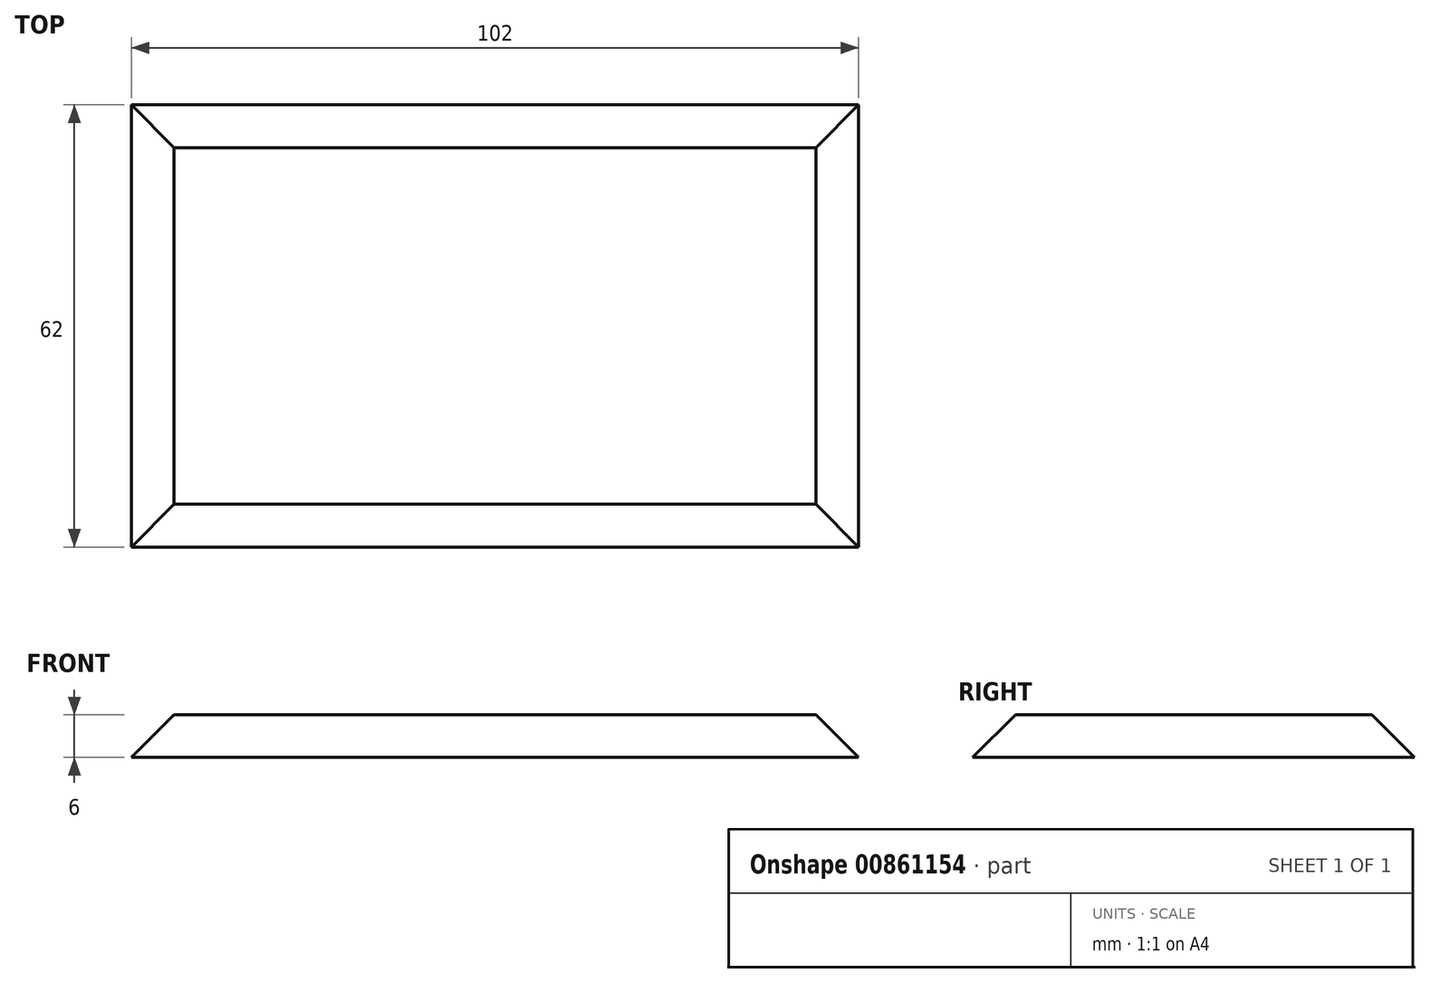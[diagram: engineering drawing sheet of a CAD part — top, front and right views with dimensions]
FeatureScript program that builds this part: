
annotation { "Feature Type Name" : "Feature", "Feature Type Description" : "" }
export const myFeature = defineFeature(function(context is Context, id is Id, definition is map)
    precondition{}
    {
        {
            var Q0;
            Q0=qCreatedBy(makeId("Top.planeOp"),FACE);
            var sketch = newSketch(context, id + "F0", { "sketchPlane" : qUnion([Q0])});
            skLineSegment(sketch, "E0.bottom", {"start": v(0, 0) * mm, "end": v(102, 0) * mm});
            skLineSegment(sketch, "E0.top", {"start": v(0, 62) * mm, "end": v(102, 62) * mm});
            skLineSegment(sketch, "E0.left", {"start": v(0, 0) * mm, "end": v(0, 62) * mm});
            skLineSegment(sketch, "E0.right", {"start": v(102, 0) * mm, "end": v(102, 62) * mm});
            skSolve(sketch);
        }
        {
            var Q0;
            Q0=makeQuery(id+"F0.imprint","IMPRINT",FACE,{"disambiguationData":[TD([[makeQuery(id+"F0.imprint","IMPRINT",EDGE,{"derivedFrom":sQuery(id+"F0.wireOp",EDGE,"E0.bottom")}),1.0]])]});
            extrude(context, id + "F1", {"entities" : qUnion([Q0]), "depth" : 6 * mm, "offsetDistance" : 25 * mm});
        }
        {
            var Q0;
            Q0=makeQuery(id+"F1.opExtrude","CAP_EDGE",EDGE,{"disambiguationData":[OSD([sQuery(id+"F0.wireOp",EDGE,"E0.bottom")])],"isStart":false});
            var Q1;
            Q1=makeQuery(id+"F1.opExtrude","CAP_EDGE",EDGE,{"disambiguationData":[OSD([sQuery(id+"F0.wireOp",EDGE,"E0.right")])],"isStart":false});
            var Q2;
            Q2=makeQuery(id+"F1.opExtrude","CAP_EDGE",EDGE,{"disambiguationData":[OSD([sQuery(id+"F0.wireOp",EDGE,"E0.top")])],"isStart":false});
            var Q3;
            Q3=makeQuery(id+"F1.opExtrude","CAP_EDGE",EDGE,{"disambiguationData":[OSD([sQuery(id+"F0.wireOp",EDGE,"E0.left")])],"isStart":false});
            chamfer(context, id + "F2", {"entities" : qUnion([Q0, Q1, Q2, Q3]), "width" : 6 * mm, "tangentPropagation" : true});
        }
    });
